# Revit family: NRG400
name_source: partatom
category: Lighting Fixtures
units: mm (PartAtom-declared; Revit-internal decimal feet)

## family parameters
Cut with Voids When Loaded = No
Host = Face
Light Source = Yes
OmniClass Number = 23.80.70.11
OmniClass Title = Luminaries for Internal Lighting
Part Type = Normal
Room Calculation Point = No
Round Connector Dimension = Use Diameter
Shared = No

## types (1)
- NRG 400
    Color Filter = 16777215
    Default Elevation = 48"
    Description = Use for building entrances, eaves, hallways, stairwells, corridors. HPS is excellent outdoors while the fluorescent systems provide great color indoors or outdoors..
    Dimming Lamp Color Temperature Shift = <None>
    Emit Shape Visible in Rendering = No
    Emit from Circle Diameter = 4"
    Finish = Bronze
    Finish2 = Bronze
    Lamp = One
    Light Source Symbol Size = 4"
    Manufacturer = EXO
    Model = NRG 400
    Opal lens = Etched Glass
    URL = https://www.currentlighting.com
    Wattage Comments = 120W

## geometry (parser evidence)
native form markers: Blend x1, Sweep x2
no freeform markers — native parametric forms only
